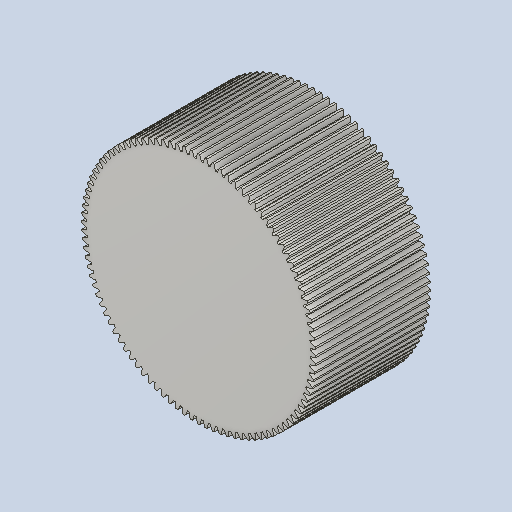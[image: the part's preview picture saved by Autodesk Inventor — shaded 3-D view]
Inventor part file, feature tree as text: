
AUTODESK INVENTOR PART (.ipt)
format: ipt  version: 2024.2 (Build 282272000, 272)  size: 528,896 bytes
history: native  units: mm (DEFAULTED — no unit token found)
features: plane x3, other x3, extrude x1, sketch x1
ambient origin geometry x8: Origin, YZ Plane, XZ Plane, XY Plane, X Axis, Y Axis, Z Axis, Center Point
bodies: Solid1 (feature_tree)
feature tree (8):
  extrude  "Extrusion1"  Depth=16.0mm TaperAngle=0.0deg
  plane  "Work Plane2"
  plane  "Work Plane8"
  plane  "Work Plane9"
  other  "Цилиндрическое зубчатое зацепление"
  sketch  "Sketch1"  dims[d0=32.64mm d1=16.0mm d2=0.0mm d3=32.0mm d4=10.0mm d5=0.0mm d16=32.0mm d17=0.0mm d34=0.314159mm d39=0.0mm d41=0.0mm d43=32.0mm d46=32.0mm d47=0.0mm d48=0.0mm]
  other  "Srf1"
  other  "Средний диаметр"
